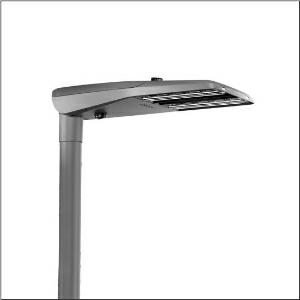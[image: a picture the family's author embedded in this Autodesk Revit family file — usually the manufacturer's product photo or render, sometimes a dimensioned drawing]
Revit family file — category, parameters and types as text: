
# Revit family: streetlight_sl_11_iq_midi___pc-l_5xc3e21y08me_ec69
name_source: partatom
category: Lighting Fixtures
units: mm (PartAtom-declared; Revit-internal decimal feet)

## family parameters
Cut with Voids When Loaded = No
Host = Face
Light Source = No
Part Type = Normal
Room Calculation Point = No
Round Connector Dimension = Use Diameter
Shared = No

## types (1)
- --- (1 x LED, 12730 lm, 122.8 W, 2200K)
    Apparent Load = 123 VA
    CIE Flux Codes = 37 73 96 100 100
    Color Rendering = 70
    Color Temperature = 2200K
    Default Elevation = 1800 mm
    Description = Streetlight SL 11 iQ midi, mast luminaire, primary light control with 3 zone facetted reflector, of plastic, silver coated, highly specular, primary optical cover: cover, of PMMA, transparent, light distribution: PC-L, light emission: direct distribution, primary light characteristic: asymmetric, left, installation type: post-top, side-entry, lamps: LED, High Power LED, rated values: 12.730lm | 122,8W | 103,7lm/W (begin service life); end service life: 12.730lm | 130,2W; at 50% lumin. flux: 6.365lm | 56W | 113,7lm/W, colour temperature: 2200K, colour rendering: CRI > 70, light colour: 722, light setting 1 begin service life: 100% | 12.730lm | 122,8W | 103,7lm/W | 2.200K, light setting 1 end service life: 130,2W, further light settings possible, control: pre-setting: logarithmic dimming characteristic, Street-Remote, Auto-Match, Temp-Guard, Lumen-Switch, Night-Set, Smart-Wire, Light-Fading, Desk-Remote (wireless, voltage-free reading and setting of iQ features in the workshop via application-optimized NFC function/RFID function), optimised constant luminous flux control (CLO 2.0), with cable H07RN-F 5x 1.5mm², mains connection: 230..240V, AC, 50/60Hz, connection cable pre-assembled, cable length: 12,5m, luminaire housing, of diecast aluminium, powder-coated, Siteco® metallic grey (DB 702S), please order mast flange separately, inclination adjustable without tools: 0°, 5°, 10°, 15° (post-top) | 0°, -5°, -10°, -15° (side-entry), sealing non-destructively replaceable, multi-level sealing system, length: 780mm, width: 376mm, height: 118mm, mast flange for spigot size: 42mm (side-entry): 5XC10008XM4, 60/48mm (side-entry/post-top): 5XC10108XM2, 76/60mm (side-entry/post-top): 5XC10108XM1, equipment: Power, Smart Interface below and above, protection rating (complete): IP66, insulation class (complete): insulation class II (safety insulation), certification: CE, ENEC, ENEC+, VDE, UKCA, impact resistance: IK10, permissible operating ambient temperature for outdoor applications: -25..+50°C, standard-compliant lighting for roads and squares, Environmental Product Declaration (EPD) tested and certified by an independent institute, packaging unit: 1 piece

Light Distribution: PC-L
    Height = 118 mm
    Lamp = 1 x LED
    Lamp Light Flux = 12730 lm
    Lamp Power = 122.8 W
    Lamp count = 1
    Length = 780 mm
    Luminous efficacy = 104 lm/W
    Manufacturer = Siteco
    ModVariant = No
    Model = 5XC3E21Y08ME
    Number of Poles = 1
    OnlyDefault = Yes
    Power Factor = 1
    Product Name = Streetlight SL 11 iQ midi | PC-L
    Product group = mast luminaire | pylon top
    ProductGroupID = 6100
    Protection Class = Protection class II
    Protection Degree = IP 66
    RLX_Detail_Level = 1
    RLX_Emergency_Light_Flux = 0 lm
    RLX_Emergency_Type = 0
    RLX_Emergency_Type_DB = No
    RlxData = <blob elided: 73665 chars, md5=389b0abe>
    Socket = socket
    Standby Power = 0 W
    System Light Flux = 12729 lm
    System Power = 123 W
    Type Comments = factory setting: luminous flux: 100 % | dim-lin: 254 | 553 mA
    Type Image = l_1004429.jpg
    URL = http://relux.com
    VarID = @adj_126688
    Voltage = 0 V
    Weight = 0.00 kg
    Width = 376 mm

## geometry (parser evidence)
native form markers: Blend x4, Sweep x12
no freeform markers — native parametric forms only
